# Revit family: Azumi Reader
name_source: partatom
category: Lighting Fixtures
revit_build: Autodesk Revit 2018 (Build: 20170927_1515(x64)
units: mm (PartAtom-declared; Revit-internal decimal feet)

## family parameters
Always vertical = Yes
Cut with Voids When Loaded = No
Host = Wall
Light Source = No
OmniClass Number = 23.80.70.00
OmniClass Title = Lighting
Part Type = Normal
Room Calculation Point = No
Round Connector Dimension = Use Diameter
Shared = No

## types (2) — shared parameters
Apparent Load = 0 VA
Driver Required = No
Manufacturer = Astro Lighting Ltd
URL = www.astrolighting.com

## per-type parameters (varying)
| type | ADA compliant | Dimmable | Dimming Method | Driver Included | Efficacy (lm/w) | Electrical Class | Lamp | Light Source Fixed | Location rating | Main Finish | Main Material | Power (Watts) | Product Code | Product Location | Product Name | Product SKU |
| CE | Not Applicable | No | Not Applicable | Yes | Lamp Dependent | 1 | Incandescent | Yes | IP20 | Various | Metal - Zinc | 60W Max | 7464 | Indoor | Azumi Reader | 1142033 |
| ETL | NO |  |  |  |  | 0 |  |  | DAMP |  | Metal - Steel |  | 1234 | Bathroom |  | 1234001 |

## geometry (parser evidence)
native form markers: Sweep x2
no freeform markers — native parametric forms only
